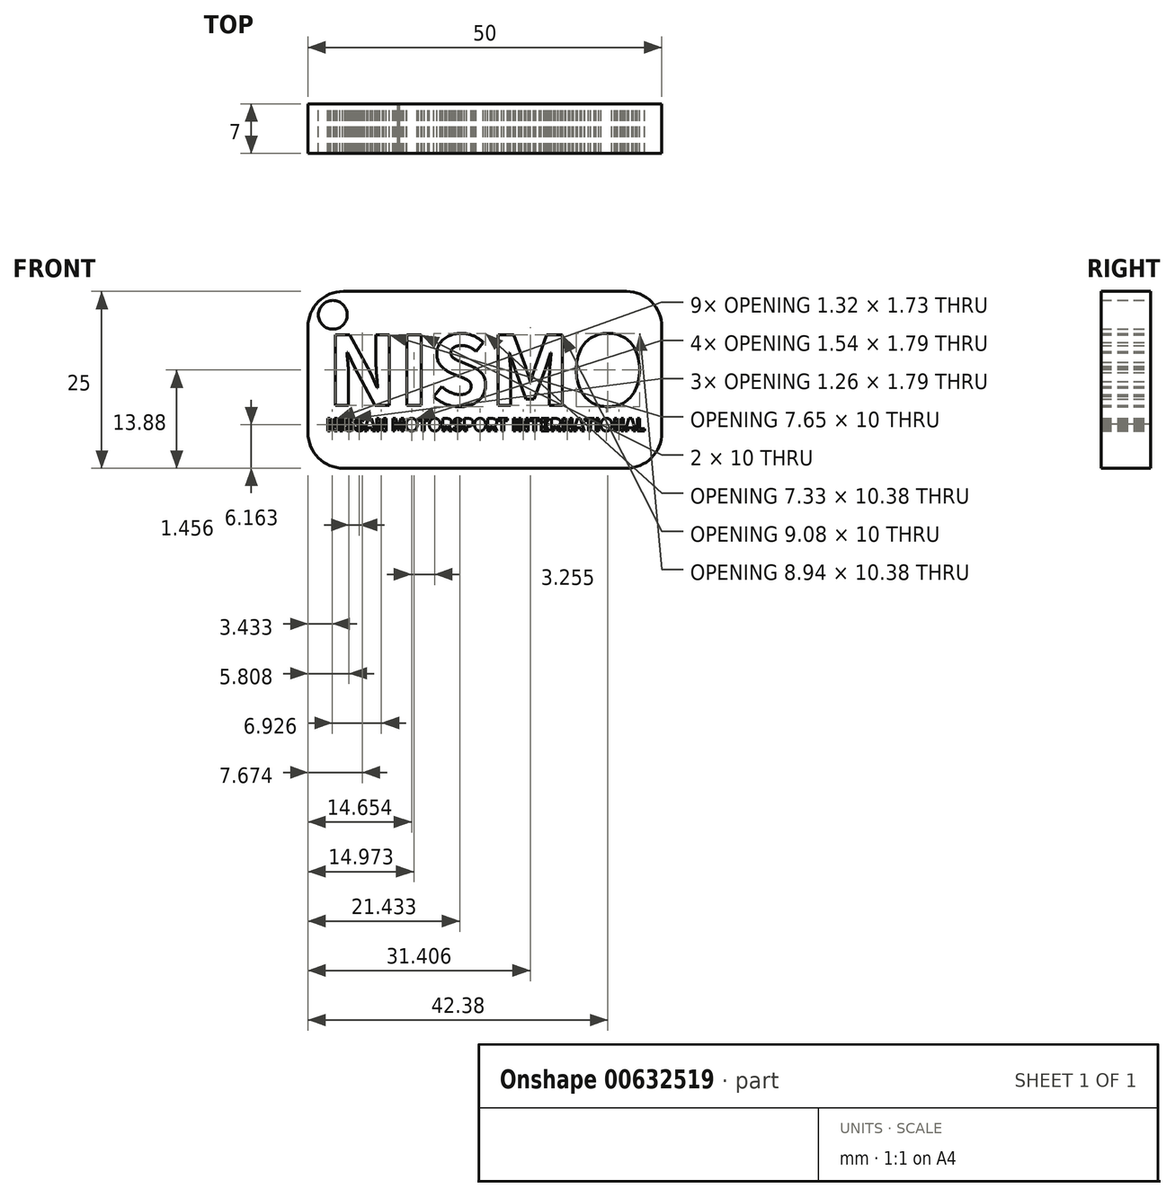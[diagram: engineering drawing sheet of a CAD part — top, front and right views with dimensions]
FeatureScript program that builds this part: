
annotation { "Feature Type Name" : "Feature", "Feature Type Description" : "" }
export const myFeature = defineFeature(function(context is Context, id is Id, definition is map)
    precondition{}
    {
        {
            var Q0;
            Q0=qCreatedBy(makeId("Front.planeOp"),FACE);
            var sketch = newSketch(context, id + "F0", { "sketchPlane" : qUnion([Q0])});
            skLineSegment(sketch, "E0.bottom", {"start": v(5, 0) * mm, "end": v(45, 0) * mm});
            skLineSegment(sketch, "E0.top", {"start": v(5, 25) * mm, "end": v(45, 25) * mm});
            skLineSegment(sketch, "E0.left", {"start": v(0, 5) * mm, "end": v(0, 20) * mm});
            skLineSegment(sketch, "E0.right", {"start": v(50, 5) * mm, "end": v(50, 20) * mm});
            skText(sketch, "E1", { "text": "NISMO", "fontName": "NotoSansCJKjp-Bold.otf"});
            skPoint(sketch, "E2.visualSharp", {"position": v(0, 25) * mm});
            skArc(sketch, "E2.filletArc", {"start": v(5, 25) * mm, "mid": v(1.46, 23.54) * mm, "end": v(0, 20) * mm});
            skPoint(sketch, "E3.visualSharp", {"position": v(50, 25) * mm});
            skArc(sketch, "E3.filletArc", {"start": v(50, 20) * mm, "mid": v(48.54, 23.54) * mm, "end": v(45, 25) * mm});
            skText(sketch, "E4", { "text": "NISSAN MOTORSPORT INTERNATIONAL", "fontName": "NotoSansCJKjp-Bold.otf"});
            skPoint(sketch, "E5.visualSharp", {"position": v(0, 0) * mm});
            skArc(sketch, "E5.filletArc", {"start": v(0, 5) * mm, "mid": v(1.46, 1.46) * mm, "end": v(5, 0) * mm});
            skPoint(sketch, "E6.visualSharp", {"position": v(50, 0) * mm});
            skArc(sketch, "E6.filletArc", {"start": v(45, 0) * mm, "mid": v(48.54, 1.46) * mm, "end": v(50, 5) * mm});
            skCircle(sketch, "E7", {"center": v(3.5, 21.7) * mm, "radius": 2.03 * mm});
            const initialGuessF0  = {"E1": [0.00262, 0.00888, 1, 0, 0.00973], "E4": [0.00256, 0.0053, 1, 0, 0.00168]};
            skSetInitialGuess(sketch, initialGuessF0);
            skSolve(sketch);
        }
        {
            var Q0;
            Q0 = qSketchRegion(id + "F0", true);
            extrude(context, id + "F1", {"entities" : qUnion([Q0]), "depth" : 7 * mm, "offsetDistance" : 25 * mm});
        }
    });
